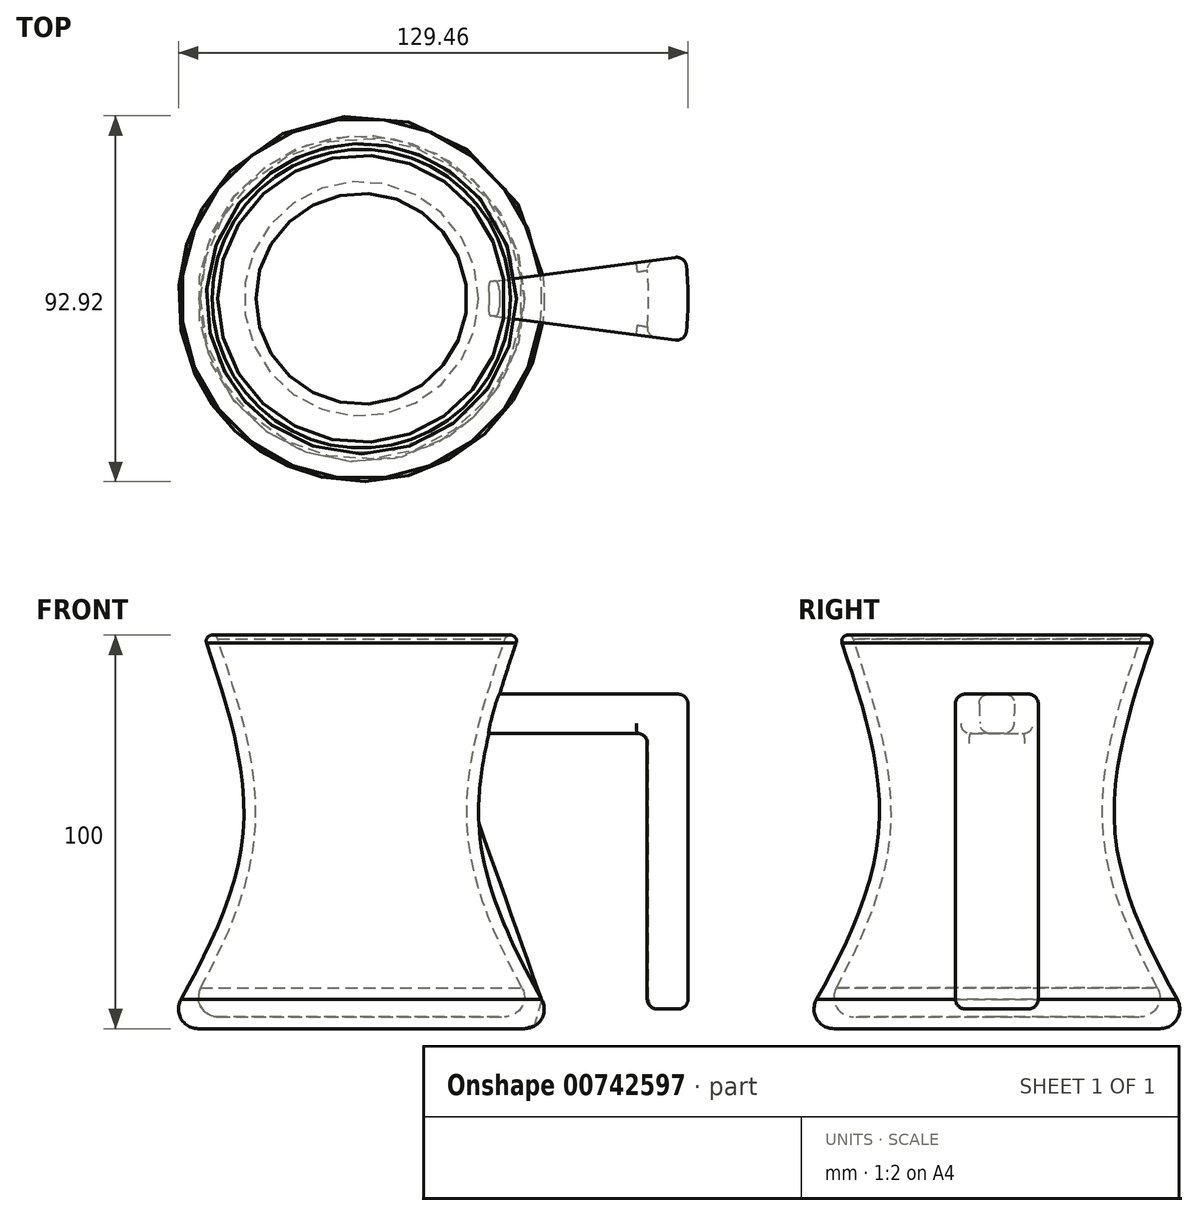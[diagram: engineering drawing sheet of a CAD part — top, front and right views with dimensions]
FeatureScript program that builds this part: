
annotation { "Feature Type Name" : "Feature", "Feature Type Description" : "" }
export const myFeature = defineFeature(function(context is Context, id is Id, definition is map)
    precondition{}
    {
        {
            var Q0;
            Q0=qCreatedBy(makeId("Top.planeOp"),FACE);
            var sketch = newSketch(context, id + "F0", { "sketchPlane" : qUnion([Q0])});
            skCircle(sketch, "E0", {"center": v(0, 0) * mm, "radius": 50 * mm});
            skSolve(sketch);
        }
        {
            var Q0;
            Q0=makeQuery(id+"F0.imprint","IMPRINT",FACE,{"disambiguationData":[TD([[makeQuery(id+"F0.imprint","IMPRINT",EDGE,{"derivedFrom":sQuery(id+"F0.wireOp",EDGE,"E0")}),1.0]])]});
            cPlane(context, id + "F1", {"entities" : qUnion([Q0]), "cplaneType" : CPlaneType.OFFSET, "offset" : 50 * mm, "width" : 150 * mm, "height" : 150 * mm});
        }
        {
            var Q0;
            Q0=qCreatedBy(id+"F1.planeOp",FACE);
            var sketch = newSketch(context, id + "F2", { "sketchPlane" : qUnion([Q0])});
            skCircle(sketch, "E1", {"center": v(0, 0) * mm, "radius": 30 * mm});
            skSolve(sketch);
        }
        {
            var Q0;
            Q0=qCreatedBy(makeId("Front.planeOp"),FACE);
            var sketch = newSketch(context, id + "F3", { "sketchPlane" : qUnion([Q0])});
            skLineSegment(sketch, "E2", {"start": v(0, 80) * mm, "end": v(0, 0) * mm, "construction": true});
            skLineSegment(sketch, "E3", {"start": v(0, 80) * mm, "end": v(33, 80) * mm, "construction": true});
            skLineSegment(sketch, "E4", {"start": v(33, 85) * mm, "end": v(83, 85) * mm});
            skLineSegment(sketch, "E5", {"start": v(83, 85) * mm, "end": v(83, 5) * mm});
            skLineSegment(sketch, "E6", {"start": v(30.5, 75) * mm, "end": v(73, 75) * mm});
            skLineSegment(sketch, "E7", {"start": v(73, 75) * mm, "end": v(73, 5) * mm});
            skLineSegment(sketch, "E8", {"start": v(73, 5) * mm, "end": v(83, 5) * mm});
            skLineSegment(sketch, "E9", {"start": v(30.5, 75) * mm, "end": v(30.5, 75) * mm});
            skLineSegment(sketch, "E10", {"start": v(33, 85) * mm, "end": v(30.5, 75) * mm});
            skLineSegment(sketch, "E11", {"start": v(33, 85) * mm, "end": v(33, 80) * mm});
            skPoint(sketch, "E12", {"position": v(33, 75) * mm});
            skSolve(sketch);
        }
        {
            var Q0;
            Q0=qCreatedBy(makeId("Top.planeOp"),FACE);
            cPlane(context, id + "F4", {"entities" : qUnion([Q0]), "cplaneType" : CPlaneType.OFFSET, "offset" : 100 * mm, "width" : 150 * mm, "height" : 150 * mm});
        }
        {
            var Q0;
            Q0=qCreatedBy(id+"F4.planeOp",FACE);
            var sketch = newSketch(context, id + "F5", { "sketchPlane" : qUnion([Q0])});
            skCircle(sketch, "E13", {"center": v(0, 0) * mm, "radius": 40 * mm});
            skSolve(sketch);
        }
        {
            var Q0;
            Q0=makeQuery(id+"F0.imprint","IMPRINT",FACE,{"disambiguationData":[TD([[makeQuery(id+"F0.imprint","IMPRINT",EDGE,{"derivedFrom":sQuery(id+"F0.wireOp",EDGE,"E0")}),1.0]])]});
            var Q1;
            Q1=makeQuery(id+"F2.imprint","IMPRINT",FACE,{"disambiguationData":[TD([[makeQuery(id+"F2.imprint","IMPRINT",EDGE,{"derivedFrom":sQuery(id+"F2.wireOp",EDGE,"E1")}),1.0]])]});
            var Q2;
            Q2=makeQuery(id+"F5.imprint","IMPRINT",FACE,{"disambiguationData":[TD([[makeQuery(id+"F5.imprint","IMPRINT",EDGE,{"derivedFrom":sQuery(id+"F5.wireOp",EDGE,"E13")}),1.0]])]});
            loft(context, id + "F6", {"sheetProfilesArray" : [{ "sheetProfileEntities" : qUnion([Q0]) }, { "sheetProfileEntities" : qUnion([Q1]) }, { "sheetProfileEntities" : qUnion([Q2]) }]});
        }
        {
            var Q0;
            Q0=makeQuery(id+"F6.opLoft","CAP_FACE",FACE,{"disambiguationData":[OSD([makeQuery(id+"F5.imprint","IMPRINT",FACE,{"disambiguationData":[TD([[makeQuery(id+"F5.imprint","IMPRINT",EDGE,{"derivedFrom":sQuery(id+"F5.wireOp",EDGE,"E13")}),1.0]])]})])],"isStart":true});
            shell(context, id + "F7", {"entities" : qUnion([Q0]), "thickness" : 3 * mm});
        }
        {
            var Q0;
            Q0=makeQuery(id+"F3.imprint","IMPRINT",FACE,{"disambiguationData":[TD([[makeQuery(id+"F3.imprint","IMPRINT",EDGE,{"derivedFrom":sQuery(id+"F3.wireOp",EDGE,"E4")}),-1.0]])]});
            var Q1;
            Q1=sQuery(id+"F3.wireOp",EDGE,"E2");
            revolve(context, id + "F8", {"operationType" : NewBodyOperationType.ADD, "surfaceOperationType" : NewSurfaceOperationType.NEW, "entities" : qUnion([Q0]), "axis" : qUnion([Q1]), "revolveType" : RevolveType.SYMMETRIC, "angle" : 15 * degree});
        }
        {
            var Q0;
            Q0=makeQuery(id+"F6.opLoft","MID_CAP_EDGE",EDGE,{"disambiguationData":[OSD([sQuery(id+"F5.wireOp",EDGE,"E13")])],"capPos":2.0});
            var Q1;
            Q1=makeQuery(id+"F7.opShell","OFFSET_EDGE",EDGE,{"disambiguationData":[OSD([sQuery(id+"F5.wireOp",EDGE,"E13")])]});
            fillet(context, id + "F9", {"entities" : qUnion([Q0, Q1]), "radius" : 1.5 * mm, "tangentPropagation" : true, "allowEdgeOverflow" : false});
        }
        {
            var Q0;
            Q0=makeQuery(id+"F6.opLoft","MID_CAP_EDGE",EDGE,{"disambiguationData":[OSD([sQuery(id+"F0.wireOp",EDGE,"E0")])],"capPos":0.0});
            var Q1;
            Q1=makeQuery(id+"F7.opShell","OFFSET_EDGE",EDGE,{"disambiguationData":[OSD([sQuery(id+"F0.wireOp",EDGE,"E0")])]});
            fillet(context, id + "F10", {"entities" : qUnion([Q0, Q1]), "radius" : 5 * mm, "tangentPropagation" : true, "allowEdgeOverflow" : false});
        }
        {
            var Q0;
            Q0=makeQuery(id+"F8.opRevolve","CAP_EDGE",EDGE,{"disambiguationData":[OSD([sQuery(id+"F3.wireOp",EDGE,"E4")])],"isStart":true});
            var Q1;
            Q1=makeQuery(id+"F8.opRevolve","CAP_EDGE",EDGE,{"disambiguationData":[OSD([sQuery(id+"F3.wireOp",EDGE,"E4")])],"isStart":false});
            var Q2;
            Q2=makeQuery(id+"F8.opRevolve","SWEPT_EDGE",EDGE,{"disambiguationData":[OSD([sQuery(id+"F3.wireOp",EDGE,"E4"),sQuery(id+"F3.wireOp",EDGE,"E5")])]});
            var Q3;
            Q3=makeQuery(id+"F8.opRevolve","CAP_EDGE",EDGE,{"disambiguationData":[OSD([sQuery(id+"F3.wireOp",EDGE,"E6")])],"isStart":false});
            var Q4;
            Q4=makeQuery(id+"F8.opRevolve","CAP_EDGE",EDGE,{"disambiguationData":[OSD([sQuery(id+"F3.wireOp",EDGE,"E6")])],"isStart":true});
            var Q5;
            Q5=makeQuery(id+"F8.opRevolve","CAP_EDGE",EDGE,{"disambiguationData":[OSD([sQuery(id+"F3.wireOp",EDGE,"E5")])],"isStart":true});
            var Q6;
            Q6=makeQuery(id+"F8.opRevolve","CAP_EDGE",EDGE,{"disambiguationData":[OSD([sQuery(id+"F3.wireOp",EDGE,"E7")])],"isStart":true});
            var Q7;
            Q7=makeQuery(id+"F8.opRevolve","CAP_EDGE",EDGE,{"disambiguationData":[OSD([sQuery(id+"F3.wireOp",EDGE,"E7")])],"isStart":false});
            var Q8;
            Q8=makeQuery(id+"F8.opRevolve","CAP_EDGE",EDGE,{"disambiguationData":[OSD([sQuery(id+"F3.wireOp",EDGE,"E5")])],"isStart":false});
            var Q9;
            Q9=makeQuery(id+"F8.opRevolve","SWEPT_FACE",FACE,{"disambiguationData":[OSD([sQuery(id+"F3.wireOp",EDGE,"E8")])]});
            var Q10;
            Q10=makeQuery(id+"F8.opRevolve","SWEPT_EDGE",EDGE,{"disambiguationData":[OSD([sQuery(id+"F3.wireOp",EDGE,"E6"),sQuery(id+"F3.wireOp",EDGE,"E7")])]});
            fillet(context, id + "F11", {"entities" : qUnion([Q0, Q1, Q2, Q3, Q4, Q5, Q6, Q7, Q8, Q9, Q10]), "radius" : 2.5 * mm, "tangentPropagation" : true, "allowEdgeOverflow" : false});
        }
    });
